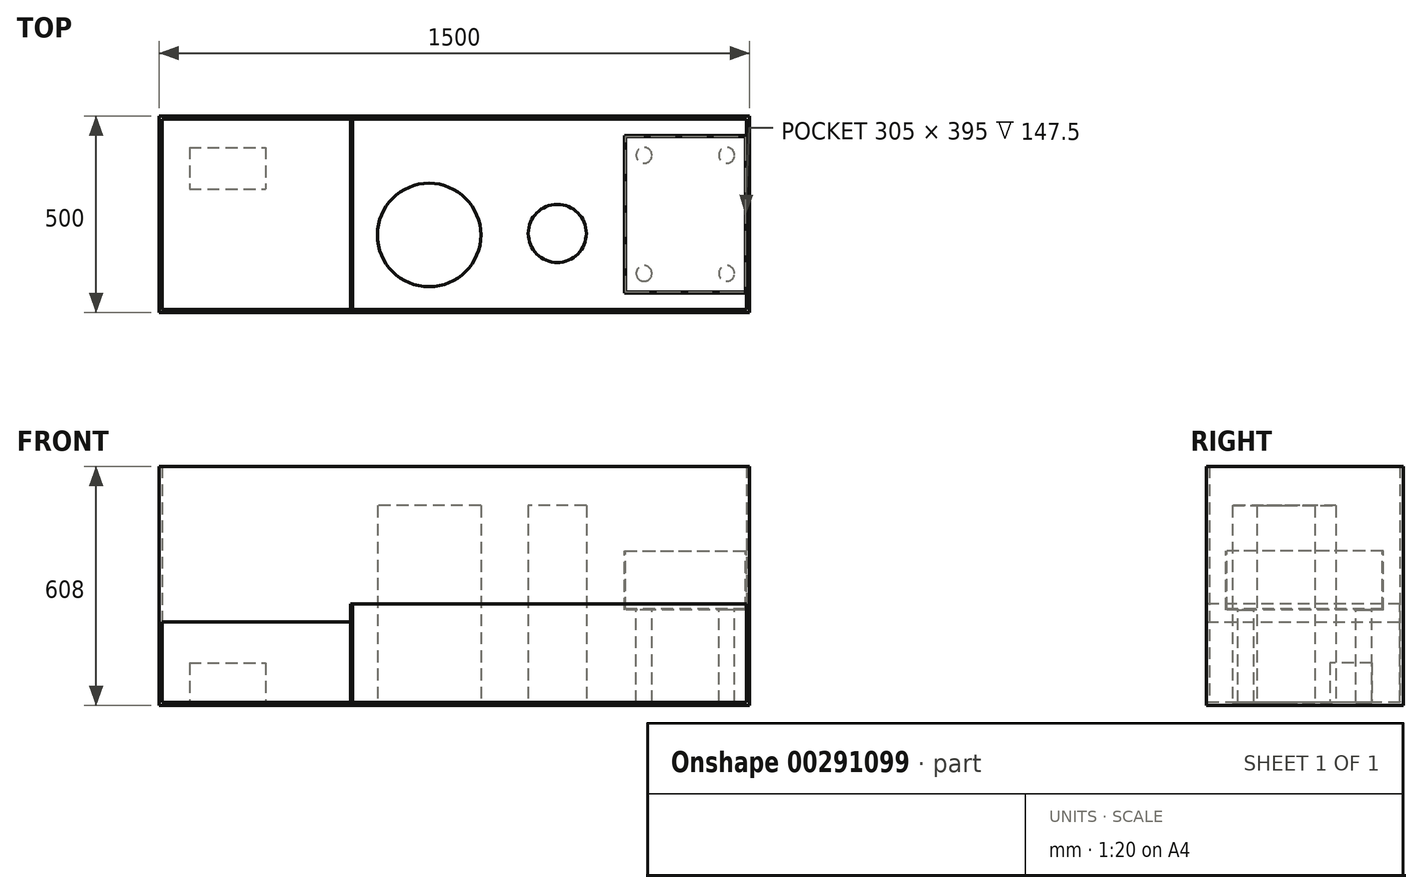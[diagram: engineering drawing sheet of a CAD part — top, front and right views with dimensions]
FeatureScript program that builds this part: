
annotation { "Feature Type Name" : "Feature", "Feature Type Description" : "" }
export const myFeature = defineFeature(function(context is Context, id is Id, definition is map)
    precondition{}
    {
        {
            var Q0;
            Q0=qCreatedBy(makeId("Top.planeOp"),FACE);
            var sketch = newSketch(context, id + "F0", { "sketchPlane" : qUnion([Q0])});
            skLineSegment(sketch, "E0.bottom", {"start": v(-750, 250) * mm, "end": v(750, 250) * mm});
            skLineSegment(sketch, "E0.top", {"start": v(-750, -250) * mm, "end": v(750, -250) * mm});
            skLineSegment(sketch, "E0.left", {"start": v(-750, 250) * mm, "end": v(-750, -250) * mm});
            skLineSegment(sketch, "E0.right", {"start": v(750, 250) * mm, "end": v(750, -250) * mm});
            skPoint(sketch, "E0.middle", {"position": v(0, 0) * mm});
            skLineSegment(sketch, "E1.bottom", {"start": v(-742, 242) * mm, "end": v(742, 242) * mm});
            skLineSegment(sketch, "E1.top", {"start": v(-742, -242) * mm, "end": v(742, -242) * mm});
            skLineSegment(sketch, "E1.left", {"start": v(-742, 242) * mm, "end": v(-742, -242) * mm});
            skLineSegment(sketch, "E1.right", {"start": v(742, 242) * mm, "end": v(742, -242) * mm});
            skSolve(sketch);
        }
        {
            var Q0;
            Q0=qSketchRegion(id+"F0",true);
            var Q1;
            Q1=makeQuery(id+"F0.imprint","IMPRINT",FACE,{"disambiguationData":[TD([[makeQuery(id+"F0.imprint","IMPRINT",EDGE,{"derivedFrom":sQuery(id+"F0.wireOp",EDGE,"E1.bottom")}),-1.0]])]});
            extrude(context, id + "F1", {"entities" : qUnion([Q0, Q1]), "oppositeDirection" : true, "depth" : 8 * mm});
        }
        {
            var Q0;
            Q0=qSketchRegion(id+"F0",true);
            extrude(context, id + "F2", {"entities" : qUnion([Q0]), "depth" : 600 * mm});
        }
        {
            var Q0;
            Q0=makeQuery(id+"F1.opExtrude","SWEPT_BODY",BODY,{"disambiguationData":[OSD([sQuery(id+"F0.wireOp",EDGE,"E0.bottom"),sQuery(id+"F0.wireOp",EDGE,"E0.top"),sQuery(id+"F0.wireOp",EDGE,"E0.left"),sQuery(id+"F0.wireOp",EDGE,"E0.right")])]});
            var Q1;
            Q1=makeQuery(id+"F2.opExtrude","SWEPT_BODY",BODY,{"disambiguationData":[OSD([sQuery(id+"F0.wireOp",EDGE,"E0.bottom"),sQuery(id+"F0.wireOp",EDGE,"E0.top"),sQuery(id+"F0.wireOp",EDGE,"E0.left"),sQuery(id+"F0.wireOp",EDGE,"E0.right"),sQuery(id+"F0.wireOp",EDGE,"E1.bottom"),sQuery(id+"F0.wireOp",EDGE,"E1.top"),sQuery(id+"F0.wireOp",EDGE,"E1.left"),sQuery(id+"F0.wireOp",EDGE,"E1.right")])]});
            booleanBodies(context, id + "F3", {"operationType" : BooleanOperationType.UNION, "tools" : qUnion([Q0, Q1])});
        }
        {
            var Q0;
            {var subQ0=sQuery(id+"F0.wireOp",EDGE,"E0.top");Q0=makeQuery(id+"F3.opBoolean","MERGE",FACE,{"derivedFrom":[makeQuery(id+"F1.opExtrude","SWEPT_FACE",FACE,{"disambiguationData":[OSD([subQ0])]}),makeQuery(id+"F2.opExtrude","SWEPT_FACE",FACE,{"disambiguationData":[OSD([subQ0])]})]});}
            var sketch = newSketch(context, id + "F4", { "sketchPlane" : qUnion([Q0])});
            skLineSegment(sketch, "E2", {"start": v(0, 0) * mm, "end": v(0, 341.46) * mm, "construction": true});
            skLineSegment(sketch, "E3.bottom", {"start": v(-258, 0) * mm, "end": v(-263, 0) * mm});
            skLineSegment(sketch, "E3.top", {"start": v(-258, 250) * mm, "end": v(-263, 250) * mm});
            skLineSegment(sketch, "E3.left", {"start": v(-258, 0) * mm, "end": v(-258, 250) * mm});
            skLineSegment(sketch, "E3.right", {"start": v(-263, 0) * mm, "end": v(-263, 250) * mm});
            skSolve(sketch);
        }
        {
            var Q0;
            Q0=qSketchRegion(id+"F4",true);
            var Q1;
            Q1=makeQuery(id+"F2.opExtrude","SWEPT_FACE",FACE,{"disambiguationData":[OSD([sQuery(id+"F0.wireOp",EDGE,"E1.bottom")])]});
            extrude(context, id + "F5", {"entities" : qUnion([Q0]), "endBound" : BoundingType.UP_TO_SURFACE, "oppositeDirection" : true, "endBoundEntityFace" : qUnion([Q1]), "depth" : 25 * mm});
        }
        {
            var Q0;
            Q0=qCreatedBy(makeId("Front.planeOp"),FACE);
            var sketch = newSketch(context, id + "F6", { "sketchPlane" : qUnion([Q0])});
            skLineSegment(sketch, "E4.0", {"start": v(472, 235) * mm, "end": v(432, 235) * mm});
            skLineSegment(sketch, "E5.0", {"start": v(742, 235) * mm, "end": v(702, 235) * mm});
            skLineSegment(sketch, "E6.bottom", {"start": v(432, 235) * mm, "end": v(742, 235) * mm});
            skLineSegment(sketch, "E6.top", {"start": v(432, 385) * mm, "end": v(742, 385) * mm});
            skLineSegment(sketch, "E6.left", {"start": v(432, 235) * mm, "end": v(432, 385) * mm});
            skLineSegment(sketch, "E6.right", {"start": v(742, 235) * mm, "end": v(742, 385) * mm});
            skSolve(sketch);
        }
        {
            var Q0;
            Q0=qSketchRegion(id+"F6",true);
            extrude(context, id + "F7", {"entities" : qUnion([Q0]), "oppositeDirection" : true, "depth" : 200 * mm, "hasSecondDirection" : true, "secondDirectionOppositeDirection" : false, "secondDirectionDepth" : 200 * mm});
        }
        {
            var Q0;
            Q0=makeQuery(id+"F7.opExtrude","SWEPT_FACE",FACE,{"disambiguationData":[OSD([sQuery(id+"F6.wireOp",EDGE,"E6.top")])]});
            shell(context, id + "F8", {"entities" : qUnion([Q0]), "thickness" : 2.5 * mm});
        }
        {
            var Q0;
            Q0=makeQuery(id+"F1.opExtrude","CAP_FACE",FACE,{"disambiguationData":[OSD([sQuery(id+"F0.wireOp",EDGE,"E0.bottom"),sQuery(id+"F0.wireOp",EDGE,"E0.top"),sQuery(id+"F0.wireOp",EDGE,"E0.left"),sQuery(id+"F0.wireOp",EDGE,"E0.right")])],"isStart":true});
            var sketch = newSketch(context, id + "F9", { "sketchPlane" : qUnion([Q0])});
            skCircle(sketch, "E7", {"center": v(-64.04, -52.45) * mm, "radius": 131.48 * mm});
            skCircle(sketch, "E8", {"center": v(261.6, -48.37) * mm, "radius": 73.85 * mm});
            skSolve(sketch);
        }
        {
            var Q0;
            Q0=qSketchRegion(id+"F9",true);
            extrude(context, id + "F10", {"entities" : qUnion([Q0]), "depth" : 500 * mm});
        }
        {
            var Q0;
            Q0=makeQuery(id+"F1.opExtrude","CAP_FACE",FACE,{"disambiguationData":[OSD([sQuery(id+"F0.wireOp",EDGE,"E0.bottom"),sQuery(id+"F0.wireOp",EDGE,"E0.top"),sQuery(id+"F0.wireOp",EDGE,"E0.left"),sQuery(id+"F0.wireOp",EDGE,"E0.right")])],"isStart":true});
            var sketch = newSketch(context, id + "F11", { "sketchPlane" : qUnion([Q0])});
            skLineSegment(sketch, "E9.bottom", {"start": v(-673.05, 170) * mm, "end": v(-479.58, 170) * mm});
            skLineSegment(sketch, "E9.top", {"start": v(-673.05, 63.71) * mm, "end": v(-479.58, 63.71) * mm});
            skLineSegment(sketch, "E9.left", {"start": v(-673.05, 170) * mm, "end": v(-673.05, 63.71) * mm});
            skLineSegment(sketch, "E9.right", {"start": v(-479.58, 170) * mm, "end": v(-479.58, 63.71) * mm});
            skSolve(sketch);
        }
        {
            var Q0;
            Q0=qSketchRegion(id+"F11",true);
            extrude(context, id + "F12", {"entities" : qUnion([Q0]), "depth" : 100 * mm});
        }
        {
            var Q0;
            Q0=makeQuery(id+"F7.opExtrude","SWEPT_FACE",FACE,{"disambiguationData":[OSD([sQuery(id+"F6.wireOp",EDGE,"E6.bottom")])]});
            var sketch = newSketch(context, id + "F13", { "sketchPlane" : qUnion([Q0])});
            skCircle(sketch, "E10", {"center": v(482, 150) * mm, "radius": 20 * mm});
            skLineSegment(sketch, "E11", {"start": v(587, 200) * mm, "end": v(587, -200) * mm, "construction": true});
            skLineSegment(sketch, "E12", {"start": v(432, 0) * mm, "end": v(742, 0) * mm, "construction": true});
            skCircle(sketch, "E13.MirrorC", {"center": v(692, 150) * mm, "radius": 20 * mm});
            skLineSegment(sketch, "E14.MirrorCS", {"start": v(742, 0) * mm, "end": v(432, 0) * mm, "construction": true});
            skCircle(sketch, "E15.MirrorC", {"center": v(692, -150) * mm, "radius": 20 * mm});
            skCircle(sketch, "E16.MirrorC", {"center": v(482, -150) * mm, "radius": 20 * mm});
            skSolve(sketch);
        }
        {
            var Q0;
            Q0 = qSketchRegion(id + "F13", true);
            var Q1;
            Q1=makeQuery(id+"F1.opExtrude","CAP_FACE",FACE,{"disambiguationData":[OSD([sQuery(id+"F0.wireOp",EDGE,"E0.bottom"),sQuery(id+"F0.wireOp",EDGE,"E0.top"),sQuery(id+"F0.wireOp",EDGE,"E0.left"),sQuery(id+"F0.wireOp",EDGE,"E0.right")])],"isStart":false});
            extrude(context, id + "F14", {"entities" : qUnion([Q0]), "operationType" : NewBodyOperationType.ADD, "endBound" : BoundingType.UP_TO_SURFACE, "endBoundEntityFace" : qUnion([Q1]), "depth" : 25 * mm});
        }
        {
            var Q0;
            Q0=qCreatedBy(makeId("Front.planeOp"),FACE);
            var sketch = newSketch(context, id + "F15", { "sketchPlane" : qUnion([Q0])});
            skLineSegment(sketch, "E17.0", {"start": v(-258, 0) * mm, "end": v(-258, 250) * mm});
            skLineSegment(sketch, "E18.0", {"start": v(742, 600) * mm, "end": v(742, 0) * mm});
            skLineSegment(sketch, "E19.bottom", {"start": v(-258, 250) * mm, "end": v(742, 250) * mm});
            skLineSegment(sketch, "E19.top", {"start": v(-258, 0) * mm, "end": v(742, 0) * mm});
            skLineSegment(sketch, "E19.left", {"start": v(-258, 250) * mm, "end": v(-258, 0) * mm});
            skLineSegment(sketch, "E19.right", {"start": v(742, 250) * mm, "end": v(742, 0) * mm});
            skLineSegment(sketch, "E20.0", {"start": v(-263, 0) * mm, "end": v(-263, 250) * mm});
            skLineSegment(sketch, "E21.0", {"start": v(-742, 600) * mm, "end": v(-742, 0) * mm});
            skLineSegment(sketch, "E22.bottom", {"start": v(-263, 204.81) * mm, "end": v(-742, 204.81) * mm});
            skLineSegment(sketch, "E22.top", {"start": v(-263, 0) * mm, "end": v(-742, 0) * mm});
            skLineSegment(sketch, "E22.left", {"start": v(-263, 204.81) * mm, "end": v(-263, 0) * mm});
            skLineSegment(sketch, "E22.right", {"start": v(-742, 204.81) * mm, "end": v(-742, 0) * mm});
            skSolve(sketch);
        }
        {
            var Q0;
            Q0 = qSketchRegion(id + "F15", true);
            var Q1;
            {var subQ0=sQuery(id+"F0.wireOp",EDGE,"E0.top");Q1=makeQuery(id+"F3.opBoolean","MERGE",FACE,{"derivedFrom":[makeQuery(id+"F1.opExtrude","SWEPT_FACE",FACE,{"disambiguationData":[OSD([subQ0])]}),makeQuery(id+"F2.opExtrude","SWEPT_FACE",FACE,{"disambiguationData":[OSD([subQ0])]})]});}
            var Q2;
            Q2=makeQuery(id+"F2.opExtrude","SWEPT_FACE",FACE,{"disambiguationData":[OSD([sQuery(id+"F0.wireOp",EDGE,"E1.bottom")])]});
            extrude(context, id + "F16", {"entities" : qUnion([Q0]), "endBound" : BoundingType.UP_TO_SURFACE, "endBoundEntityFace" : qUnion([Q1]), "depth" : 25 * mm, "hasSecondDirection" : true, "secondDirectionBound" : SecondDirectionBoundingType.UP_TO_SURFACE, "secondDirectionOppositeDirection" : true, "secondDirectionBoundEntityFace" : qUnion([Q2]), "secondDirectionDepth" : 25 * mm});
        }
    });
